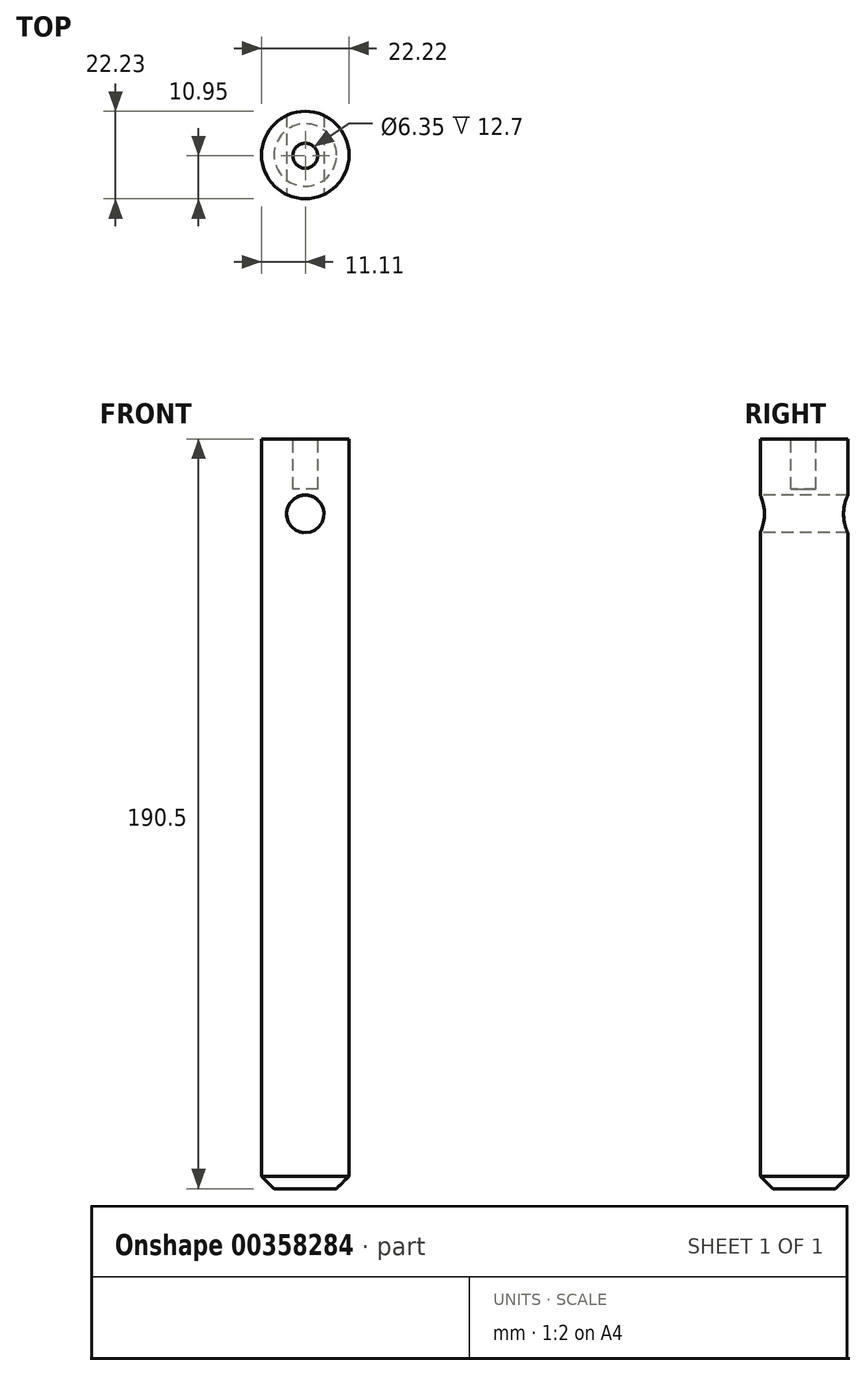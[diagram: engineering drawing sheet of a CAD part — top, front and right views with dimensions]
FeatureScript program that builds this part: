
annotation { "Feature Type Name" : "Feature", "Feature Type Description" : "" }
export const myFeature = defineFeature(function(context is Context, id is Id, definition is map)
    precondition{}
    {
        {
            var Q0;
            Q0=qCreatedBy(makeId("Top.planeOp"),FACE);
            var sketch = newSketch(context, id + "F0", { "sketchPlane" : qUnion([Q0])});
            skCircle(sketch, "E0", {"center": v(0, 0.17) * mm, "radius": 11.11 * mm});
            skSolve(sketch);
        }
        {
            var Q0;
            Q0 = qSketchRegion(id + "F0", true);
            extrude(context, id + "F1", {"entities" : qUnion([Q0]), "depth" : 190.5 * mm});
        }
        {
            var Q0;
            Q0=makeQuery(id+"F1.opExtrude","CAP_EDGE",EDGE,{"disambiguationData":[OSD([sQuery(id+"F0.wireOp",EDGE,"E0")])],"isStart":true});
            chamfer(context, id + "F2", {"entities" : qUnion([Q0]), "width" : 3.17 * mm, "tangentPropagation" : true});
        }
        {
            var Q0;
            Q0=qCreatedBy(makeId("Front.planeOp"),FACE);
            var sketch = newSketch(context, id + "F3", { "sketchPlane" : qUnion([Q0])});
            skCircle(sketch, "E1", {"center": v(0, 171.45) * mm, "radius": 4.76 * mm});
            skSolve(sketch);
        }
        {
            var Q0;
            Q0 = qSketchRegion(id + "F3", true);
            extrude(context, id + "F4", {"entities" : qUnion([Q0]), "operationType" : NewBodyOperationType.REMOVE, "oppositeDirection" : true, "depth" : 25.4 * mm, "hasSecondDirection" : true, "secondDirectionOppositeDirection" : false, "secondDirectionDepth" : 25.4 * mm});
        }
        {
            var Q0;
            Q0=makeQuery(id+"F1.opExtrude","CAP_FACE",FACE,{"disambiguationData":[OSD([sQuery(id+"F0.wireOp",EDGE,"E0")])],"isStart":false});
            var sketch = newSketch(context, id + "F5", { "sketchPlane" : qUnion([Q0])});
            skCircle(sketch, "E2", {"center": v(0, 0) * mm, "radius": 3.18 * mm});
            skSolve(sketch);
        }
        {
            var Q0;
            Q0 = qSketchRegion(id + "F5", true);
            extrude(context, id + "F6", {"entities" : qUnion([Q0]), "operationType" : NewBodyOperationType.REMOVE, "oppositeDirection" : true, "depth" : 12.7 * mm});
        }
    });
